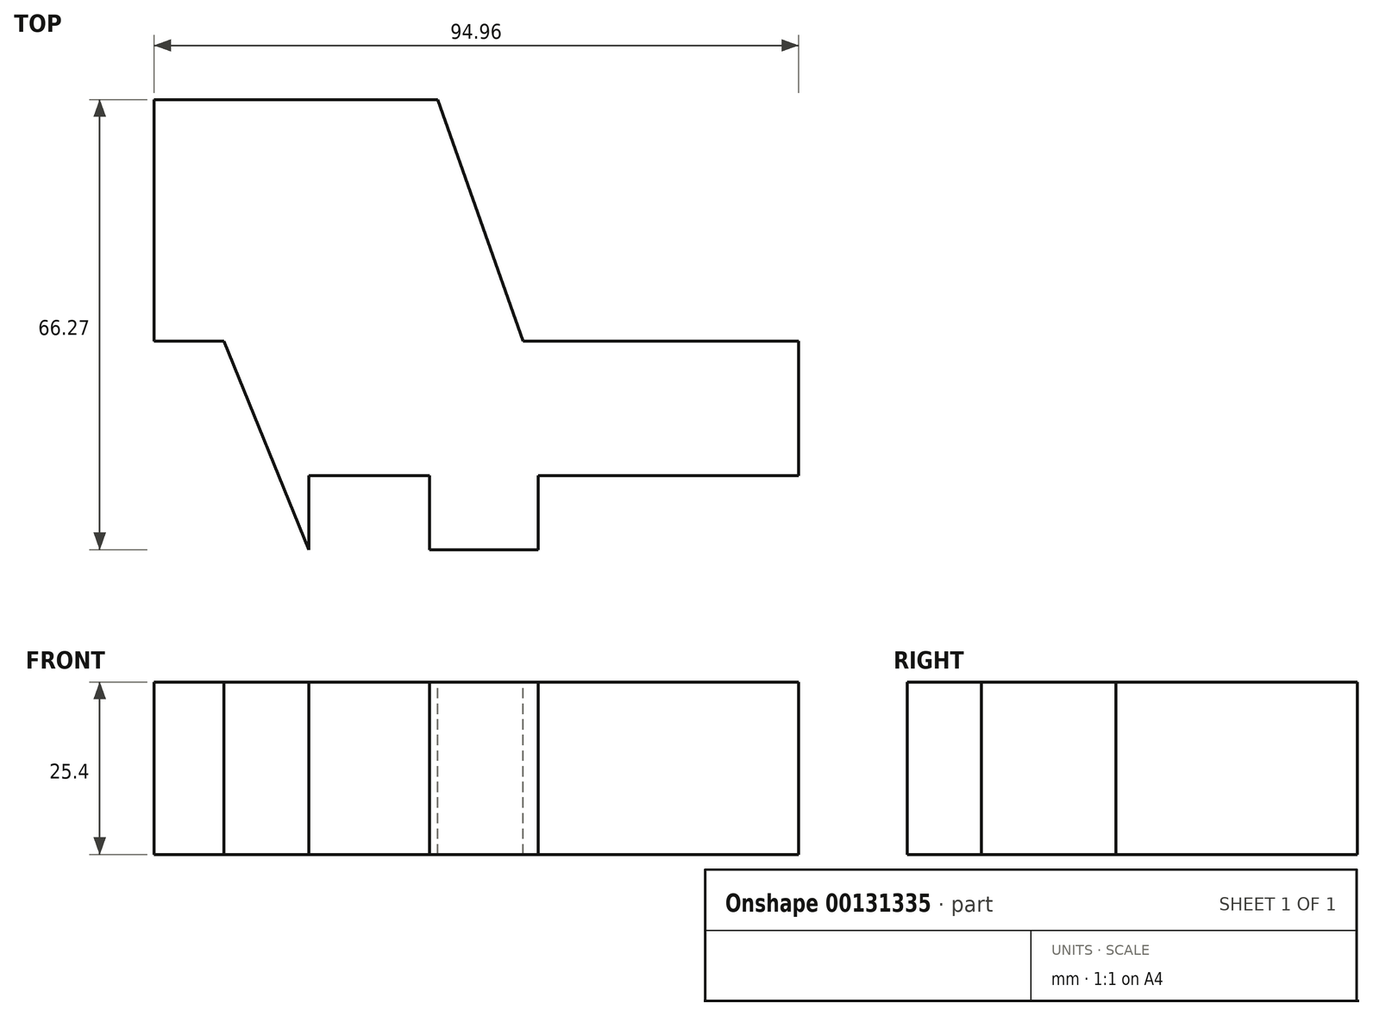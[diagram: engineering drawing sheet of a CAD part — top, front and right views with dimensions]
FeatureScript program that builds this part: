
annotation { "Feature Type Name" : "Feature", "Feature Type Description" : "" }
export const myFeature = defineFeature(function(context is Context, id is Id, definition is map)
    precondition{}
    {
        {
            var Q0;
            Q0=qCreatedBy(makeId("Top.planeOp"),FACE);
            var sketch = newSketch(context, id + "F0", { "sketchPlane" : qUnion([Q0])});
            skLineSegment(sketch, "E0", {"start": v(32.5, -11.23) * mm, "end": v(51.2, -11.23) * mm});
            skLineSegment(sketch, "E1", {"start": v(51.2, -11.23) * mm, "end": v(51.2, 8.57) * mm});
            skLineSegment(sketch, "E2", {"start": v(12.8, -11.23) * mm, "end": v(12.8, -22.14) * mm});
            skLineSegment(sketch, "E3", {"start": v(12.8, -22.14) * mm, "end": v(-3.15, -22.14) * mm});
            skLineSegment(sketch, "E4", {"start": v(-3.15, -22.14) * mm, "end": v(-3.15, -11.23) * mm});
            skLineSegment(sketch, "E5", {"start": v(-3.15, -11.23) * mm, "end": v(-20.93, -11.23) * mm});
            skLineSegment(sketch, "E6", {"start": v(-20.93, -11.23) * mm, "end": v(-20.93, -22.14) * mm});
            skLineSegment(sketch, "E7", {"start": v(-20.93, -22.14) * mm, "end": v(-33.46, 8.57) * mm});
            skLineSegment(sketch, "E8", {"start": v(-33.46, 8.57) * mm, "end": v(-43.76, 8.57) * mm});
            skLineSegment(sketch, "E9", {"start": v(12.8, -11.23) * mm, "end": v(32.5, -11.23) * mm});
            skLineSegment(sketch, "E10", {"start": v(-43.76, 8.57) * mm, "end": v(-43.76, 44.13) * mm});
            skLineSegment(sketch, "E11", {"start": v(-43.76, 44.13) * mm, "end": v(-1.94, 44.13) * mm});
            skLineSegment(sketch, "E12", {"start": v(-1.94, 44.13) * mm, "end": v(10.59, 8.57) * mm});
            skLineSegment(sketch, "E13", {"start": v(10.59, 8.57) * mm, "end": v(51.2, 8.57) * mm});
            skSolve(sketch);
        }
        {
            var Q0;
            Q0=sQuery(id+"F0.wireOp",EDGE,"E0");
            var Q1;
            Q1=sQuery(id+"F0.wireOp",EDGE,"E1");
            var Q2;
            Q2=sQuery(id+"F0.wireOp",EDGE,"E2");
            var Q3;
            Q3=sQuery(id+"F0.wireOp",EDGE,"E3");
            var Q4;
            Q4=sQuery(id+"F0.wireOp",EDGE,"E4");
            var Q5;
            Q5=sQuery(id+"F0.wireOp",EDGE,"E5");
            var Q6;
            Q6=sQuery(id+"F0.wireOp",EDGE,"E6");
            var Q7;
            Q7=sQuery(id+"F0.wireOp",EDGE,"E7");
            var Q8;
            Q8=sQuery(id+"F0.wireOp",EDGE,"E8");
            var Q9;
            Q9=sQuery(id+"F0.wireOp",EDGE,"E9");
            var Q10;
            Q10=sQuery(id+"F0.wireOp",EDGE,"E10");
            var Q11;
            Q11=sQuery(id+"F0.wireOp",EDGE,"E11");
            var Q12;
            Q12=sQuery(id+"F0.wireOp",EDGE,"E12");
            var Q13;
            Q13=sQuery(id+"F0.wireOp",EDGE,"E13");
            extrude(context, id + "F1", {"bodyType" : ToolBodyType.SURFACE, "surfaceEntities" : qUnion([Q0, Q1, Q2, Q3, Q4, Q5, Q6, Q7, Q8, Q9, Q10, Q11, Q12, Q13]), "depth" : 25.4 * mm});
        }
    });
